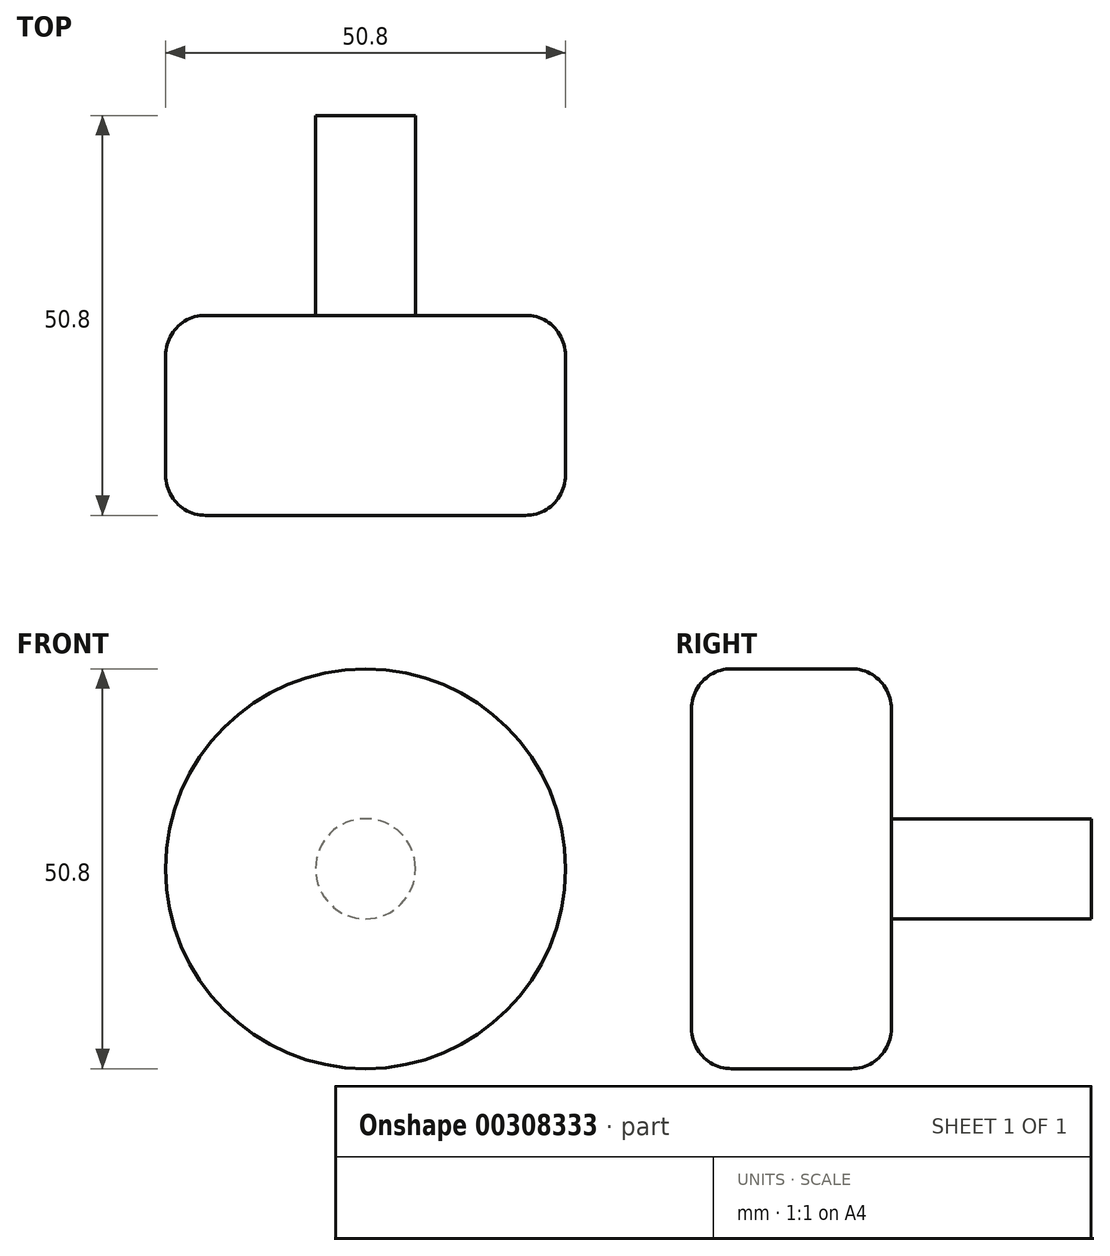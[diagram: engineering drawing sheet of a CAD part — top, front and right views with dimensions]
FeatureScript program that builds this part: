
annotation { "Feature Type Name" : "Feature", "Feature Type Description" : "" }
export const myFeature = defineFeature(function(context is Context, id is Id, definition is map)
    precondition{}
    {
        {
            var Q0;
            Q0=qCreatedBy(makeId("Front.planeOp"),FACE);
            var sketch = newSketch(context, id + "F0", { "sketchPlane" : qUnion([Q0])});
            skCircle(sketch, "E0", {"center": v(0, 0) * mm, "radius": 25.4 * mm});
            skCircle(sketch, "E1", {"center": v(0, 0) * mm, "radius": 6.35 * mm});
            skSolve(sketch);
        }
        {
            var Q0;
            Q0=makeQuery(id+"F0.imprint","IMPRINT",FACE,{"disambiguationData":[TD([[makeQuery(id+"F0.imprint","IMPRINT",EDGE,{"derivedFrom":sQuery(id+"F0.wireOp",EDGE,"E1")}),1.0]])]});
            var Q1;
            Q1=makeQuery(id+"F0.imprint","IMPRINT",FACE,{"disambiguationData":[TD([[makeQuery(id+"F0.imprint","IMPRINT",EDGE,{"derivedFrom":sQuery(id+"F0.wireOp",EDGE,"E0")}),1.0]])]});
            extrude(context, id + "F1", {"entities" : qUnion([Q0, Q1]), "depth" : 25.4 * mm});
        }
        {
            var Q0;
            Q0=makeQuery(id+"F1.opExtrude","CAP_EDGE",EDGE,{"disambiguationData":[OSD([sQuery(id+"F0.wireOp",EDGE,"E0")])],"isStart":false});
            var Q1;
            Q1=makeQuery(id+"F1.opExtrude","CAP_EDGE",EDGE,{"disambiguationData":[OSD([sQuery(id+"F0.wireOp",EDGE,"E0")])],"isStart":true});
            fillet(context, id + "F2", {"entities" : qUnion([Q0, Q1]), "radius" : 5.08 * mm, "tangentPropagation" : true, "allowEdgeOverflow" : false});
        }
        {
            var Q0;
            Q0=makeQuery(id+"F0.imprint","IMPRINT",FACE,{"disambiguationData":[TD([[makeQuery(id+"F0.imprint","IMPRINT",EDGE,{"derivedFrom":sQuery(id+"F0.wireOp",EDGE,"E1")}),1.0]])]});
            extrude(context, id + "F3", {"entities" : qUnion([Q0]), "operationType" : NewBodyOperationType.ADD, "depth" : -25.4 * mm});
        }
    });
